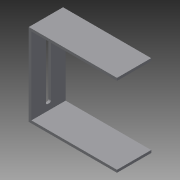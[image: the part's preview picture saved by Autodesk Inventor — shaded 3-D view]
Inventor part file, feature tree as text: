
AUTODESK INVENTOR PART (.ipt)
format: ipt  version: 2015 (Build 190159000, 159)  size: 115,712 bytes
history: native  units: mm
features: extrude x4, sketch x4, other x1, fillet x1
ambient origin geometry x8: Origin, YZ Plane, XZ Plane, XY Plane, X Axis, Y Axis, Z Axis, Center Point
bodies: Body1 (feature_tree)
feature tree (10):
  other  "ソリッド1"
  extrude  "押し出し1"  Depth=50.0mm
  extrude  "押し出し2"  Depth=20.0mm
  extrude  "押し出し3"  Depth=1.5mm TaperAngle=0.0deg
  extrude  "押し出し4"  Depth=48.0mm
  fillet  "フィレット1"  Radius=20.0mm
  sketch  "スケッチ1"
  sketch  "スケッチ2"
  sketch  "スケッチ4"
  sketch  "スケッチ5"
